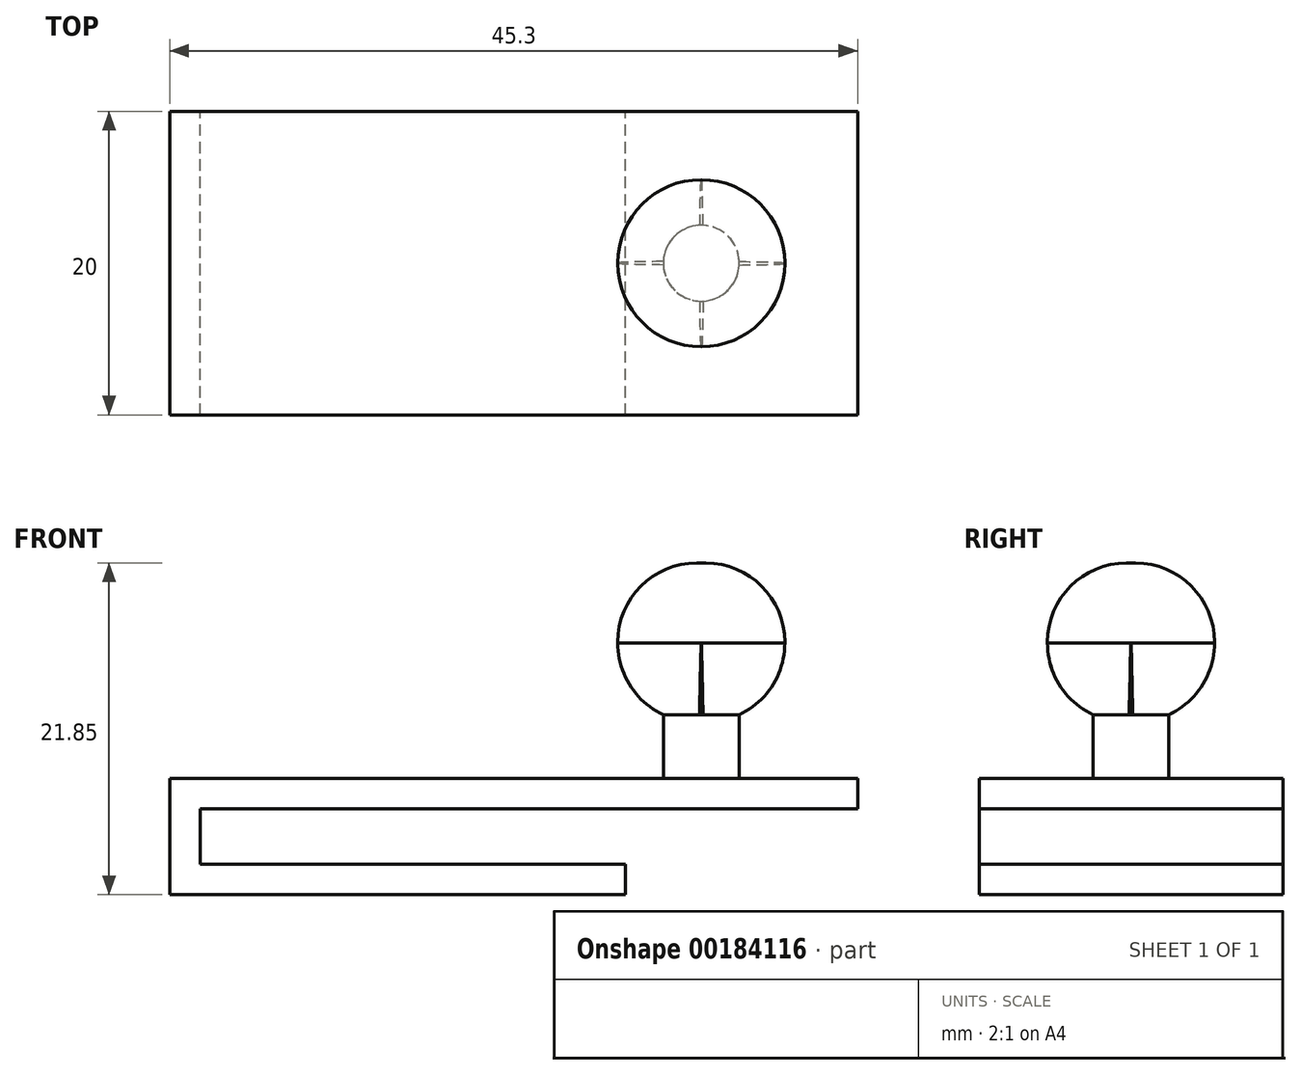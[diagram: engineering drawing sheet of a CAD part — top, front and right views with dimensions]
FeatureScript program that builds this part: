
annotation { "Feature Type Name" : "Feature", "Feature Type Description" : "" }
export const myFeature = defineFeature(function(context is Context, id is Id, definition is map)
    precondition{}
    {
        {
            var Q0;
            Q0=qCreatedBy(makeId("Front.planeOp"),FACE);
            var sketch = newSketch(context, id + "F0", { "sketchPlane" : qUnion([Q0])});
            skLineSegment(sketch, "E0.bottom", {"start": v(0, 0) * mm, "end": v(30, 0) * mm});
            skLineSegment(sketch, "E0.top", {"start": v(2, 2) * mm, "end": v(30, 2) * mm});
            skLineSegment(sketch, "E0.right", {"start": v(30, 0) * mm, "end": v(30, 2) * mm});
            skPoint(sketch, "E1", {"position": v(2, 2) * mm});
            skLineSegment(sketch, "E2", {"start": v(2, 2) * mm, "end": v(2, 5.65) * mm});
            skLineSegment(sketch, "E3", {"start": v(2, 5.65) * mm, "end": v(45.3, 5.65) * mm});
            skLineSegment(sketch, "E4", {"start": v(45.3, 5.65) * mm, "end": v(45.3, 7.65) * mm});
            skLineSegment(sketch, "E5", {"start": v(45.3, 7.65) * mm, "end": v(0, 7.65) * mm});
            skLineSegment(sketch, "E6", {"start": v(0, 7.65) * mm, "end": v(0, 0) * mm});
            skSolve(sketch);
        }
        {
            var Q0;
            Q0=makeQuery(id+"F0.imprint","IMPRINT",FACE,{"disambiguationData":[TD([[makeQuery(id+"F0.imprint","IMPRINT",EDGE,{"derivedFrom":sQuery(id+"F0.wireOp",EDGE,"E0.bottom")}),1.0]])]});
            extrude(context, id + "F1", {"entities" : qUnion([Q0]), "endBound" : BoundingType.SYMMETRIC, "depth" : 20 * mm});
        }
        {
            var Q0;
            Q0=makeQuery(id+"F1.opExtrude","SWEPT_FACE",FACE,{"disambiguationData":[OSD([sQuery(id+"F0.wireOp",EDGE,"E5")])]});
            var sketch = newSketch(context, id + "F2", { "sketchPlane" : qUnion([Q0])});
            skCircle(sketch, "E7", {"center": v(35, 0) * mm, "radius": 2.5 * mm});
            skSolve(sketch);
        }
        {
            var Q0;
            Q0=qSketchRegion(id+"F2",true);
            extrude(context, id + "F3", {"entities" : qUnion([Q0]), "operationType" : NewBodyOperationType.ADD, "depth" : 4.2 * mm});
        }
        {
            var Q0;
            Q0=makeQuery(id+"F3.opExtrude","CAP_FACE",FACE,{"disambiguationData":[OSD([sQuery(id+"F2.wireOp",EDGE,"E7")])],"isStart":false});
            var sketch = newSketch(context, id + "F4", { "sketchPlane" : qUnion([Q0])});
            skLineSegment(sketch, "E8.bottom", {"start": v(40.5, 5.5) * mm, "end": v(29.5, 5.5) * mm});
            skLineSegment(sketch, "E8.top", {"start": v(40.5, -5.5) * mm, "end": v(29.5, -5.5) * mm});
            skLineSegment(sketch, "E8.left", {"start": v(40.5, 5.5) * mm, "end": v(40.5, -5.5) * mm});
            skLineSegment(sketch, "E8.right", {"start": v(29.5, 5.5) * mm, "end": v(29.5, -5.5) * mm});
            skPoint(sketch, "E8.middle", {"position": v(35, 0) * mm});
            skSolve(sketch);
        }
        {
            var Q0;
            Q0=qSketchRegion(id+"F4",true);
            extrude(context, id + "F5", {"entities" : qUnion([Q0]), "operationType" : NewBodyOperationType.ADD, "depth" : 10 * mm});
        }
        {
            var Q0;
            Q0=makeQuery(id+"F5.opExtrude","SWEPT_EDGE",EDGE,{"disambiguationData":[OSD([sQuery(id+"F4.wireOp",EDGE,"E8.top"),sQuery(id+"F4.wireOp",EDGE,"E8.right")])]});
            var Q1;
            Q1=makeQuery(id+"F5.opExtrude","SWEPT_EDGE",EDGE,{"disambiguationData":[OSD([sQuery(id+"F4.wireOp",EDGE,"E8.top"),sQuery(id+"F4.wireOp",EDGE,"E8.left")])]});
            var Q2;
            Q2=makeQuery(id+"F5.opExtrude","SWEPT_EDGE",EDGE,{"disambiguationData":[OSD([sQuery(id+"F4.wireOp",EDGE,"E8.bottom"),sQuery(id+"F4.wireOp",EDGE,"E8.left")])]});
            var Q3;
            Q3=makeQuery(id+"F5.opExtrude","SWEPT_EDGE",EDGE,{"disambiguationData":[OSD([sQuery(id+"F4.wireOp",EDGE,"E8.bottom"),sQuery(id+"F4.wireOp",EDGE,"E8.right")])]});
            fillet(context, id + "F6", {"entities" : qUnion([Q0, Q1, Q2, Q3]), "radius" : 5.5 * mm, "tangentPropagation" : true, "allowEdgeOverflow" : false});
        }
        {
            var Q0;
            {var subQ0=sQuery(id+"F4.wireOp",EDGE,"E8.left");var subQ1=sQuery(id+"F4.wireOp",EDGE,"E8.bottom");Q0=makeQuery(id+"F6.opFillet","BLEND_EDGE",EDGE,{"blendedFrom":[makeQuery(id+"F5.opExtrude","SWEPT_EDGE",EDGE,{"disambiguationData":[OSD([subQ1,subQ0])]}),makeQuery(id+"F5.opExtrude","CAP_FACE",FACE,{"disambiguationData":[OSD([subQ1,sQuery(id+"F4.wireOp",EDGE,"E8.top"),subQ0,sQuery(id+"F4.wireOp",EDGE,"E8.right")])],"isStart":false})],"blendedInto":[makeQuery(id+"F5.opExtrude","CAP_FACE",FACE,{"disambiguationData":[OSD([subQ1,sQuery(id+"F4.wireOp",EDGE,"E8.top"),subQ0,sQuery(id+"F4.wireOp",EDGE,"E8.right")])],"isStart":false})]});}
            var Q1;
            {var subQ0=sQuery(id+"F4.wireOp",EDGE,"E8.left");var subQ1=sQuery(id+"F4.wireOp",EDGE,"E8.bottom");Q1=makeQuery(id+"F6.opFillet","BLEND_EDGE",EDGE,{"blendedFrom":[makeQuery(id+"F5.opExtrude","SWEPT_EDGE",EDGE,{"disambiguationData":[OSD([subQ1,subQ0])]}),makeQuery(id+"F5.opExtrude","CAP_FACE",FACE,{"disambiguationData":[OSD([subQ1,sQuery(id+"F4.wireOp",EDGE,"E8.top"),subQ0,sQuery(id+"F4.wireOp",EDGE,"E8.right")])],"isStart":true})],"blendedInto":[makeQuery(id+"F5.opExtrude","CAP_FACE",FACE,{"disambiguationData":[OSD([subQ1,sQuery(id+"F4.wireOp",EDGE,"E8.top"),subQ0,sQuery(id+"F4.wireOp",EDGE,"E8.right")])],"isStart":true})]});}
            fillet(context, id + "F7", {"entities" : qUnion([Q0, Q1]), "radius" : 5.2 * mm, "tangentPropagation" : true, "allowEdgeOverflow" : false});
        }
    });
